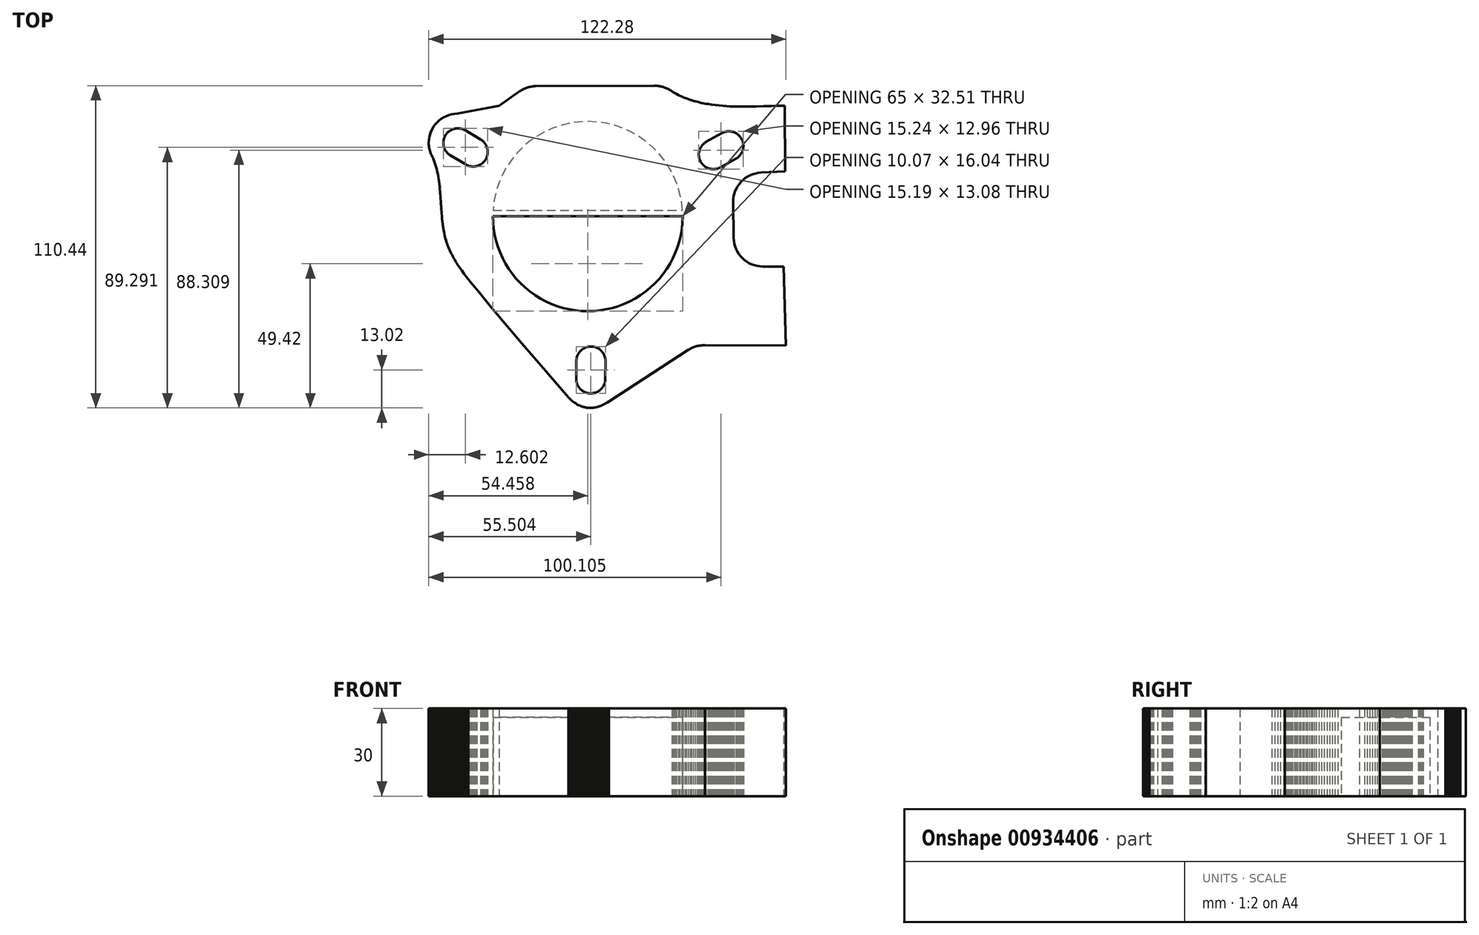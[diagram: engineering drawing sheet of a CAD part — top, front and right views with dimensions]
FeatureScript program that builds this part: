
annotation { "Feature Type Name" : "Feature", "Feature Type Description" : "" }
export const myFeature = defineFeature(function(context is Context, id is Id, definition is map)
    precondition{}
    {
        {
            var Q0;
            Q0=qCreatedBy(makeId("Top.planeOp"),FACE);
            var sketch = newSketch(context, id + "F0", { "sketchPlane" : qUnion([Q0])});
            skArc(sketch, "E0", {"start": v(-6.68, 42.95) * mm, "mid": v(-29.66, 33.43) * mm, "end": v(-39.18, 10.45) * mm});
            skArc(sketch, "E1", {"start": v(-39.18, 10.45) * mm, "mid": v(-29.66, -12.54) * mm, "end": v(-6.68, -22.05) * mm});
            skArc(sketch, "E2", {"start": v(-6.68, -22.05) * mm, "mid": v(16.3, -12.54) * mm, "end": v(25.82, 10.45) * mm});
            skArc(sketch, "E3", {"start": v(25.82, 10.45) * mm, "mid": v(16.3, 33.43) * mm, "end": v(-6.68, 42.95) * mm});
            skLineSegment(sketch, "E4", {"start": v(38.78, 27.25) * mm, "end": v(44.05, 30.21) * mm});
            skLineSegment(sketch, "E5", {"start": v(44.05, 30.21) * mm, "end": v(44.26, 30.34) * mm});
            skLineSegment(sketch, "E6", {"start": v(44.26, 30.34) * mm, "end": v(44.46, 30.47) * mm});
            skLineSegment(sketch, "E7", {"start": v(44.46, 30.47) * mm, "end": v(44.65, 30.61) * mm});
            skLineSegment(sketch, "E8", {"start": v(44.65, 30.61) * mm, "end": v(44.84, 30.76) * mm});
            skLineSegment(sketch, "E9", {"start": v(44.84, 30.76) * mm, "end": v(45.02, 30.92) * mm});
            skLineSegment(sketch, "E10", {"start": v(45.02, 30.92) * mm, "end": v(45.2, 31.1) * mm});
            skLineSegment(sketch, "E11", {"start": v(45.2, 31.1) * mm, "end": v(45.35, 31.27) * mm});
            skLineSegment(sketch, "E12", {"start": v(45.35, 31.27) * mm, "end": v(45.51, 31.45) * mm});
            skLineSegment(sketch, "E13", {"start": v(45.51, 31.45) * mm, "end": v(45.66, 31.65) * mm});
            skLineSegment(sketch, "E14", {"start": v(45.66, 31.65) * mm, "end": v(45.8, 31.85) * mm});
            skLineSegment(sketch, "E15", {"start": v(45.8, 31.85) * mm, "end": v(45.93, 32.06) * mm});
            skLineSegment(sketch, "E16", {"start": v(45.93, 32.06) * mm, "end": v(46.04, 32.28) * mm});
            skLineSegment(sketch, "E17", {"start": v(46.04, 32.28) * mm, "end": v(46.15, 32.5) * mm});
            skLineSegment(sketch, "E18", {"start": v(46.15, 32.5) * mm, "end": v(46.25, 32.74) * mm});
            skLineSegment(sketch, "E19", {"start": v(46.25, 32.74) * mm, "end": v(46.34, 32.98) * mm});
            skLineSegment(sketch, "E20", {"start": v(46.34, 32.98) * mm, "end": v(46.41, 33.22) * mm});
            skArc(sketch, "E21", {"start": v(46.41, 33.22) * mm, "mid": v(45.96, 37.02) * mm, "end": v(42.95, 39.39) * mm});
            skLineSegment(sketch, "E22", {"start": v(42.95, 39.39) * mm, "end": v(42.7, 39.45) * mm});
            skLineSegment(sketch, "E23", {"start": v(42.7, 39.45) * mm, "end": v(42.45, 39.5) * mm});
            skLineSegment(sketch, "E24", {"start": v(42.45, 39.5) * mm, "end": v(42.2, 39.54) * mm});
            skLineSegment(sketch, "E25", {"start": v(42.2, 39.54) * mm, "end": v(41.95, 39.56) * mm});
            skLineSegment(sketch, "E26", {"start": v(41.95, 39.56) * mm, "end": v(41.7, 39.57) * mm});
            skLineSegment(sketch, "E27", {"start": v(41.7, 39.57) * mm, "end": v(41.46, 39.57) * mm});
            skLineSegment(sketch, "E28", {"start": v(41.46, 39.57) * mm, "end": v(41.21, 39.56) * mm});
            skLineSegment(sketch, "E29", {"start": v(41.21, 39.56) * mm, "end": v(40.97, 39.53) * mm});
            skLineSegment(sketch, "E30", {"start": v(40.97, 39.53) * mm, "end": v(40.73, 39.5) * mm});
            skLineSegment(sketch, "E31", {"start": v(40.73, 39.5) * mm, "end": v(40.49, 39.45) * mm});
            skLineSegment(sketch, "E32", {"start": v(40.49, 39.45) * mm, "end": v(40.26, 39.39) * mm});
            skLineSegment(sketch, "E33", {"start": v(40.26, 39.39) * mm, "end": v(40.03, 39.32) * mm});
            skLineSegment(sketch, "E34", {"start": v(40.03, 39.32) * mm, "end": v(39.8, 39.24) * mm});
            skLineSegment(sketch, "E35", {"start": v(39.8, 39.24) * mm, "end": v(39.58, 39.14) * mm});
            skLineSegment(sketch, "E36", {"start": v(39.58, 39.14) * mm, "end": v(39.36, 39.04) * mm});
            skLineSegment(sketch, "E37", {"start": v(39.36, 39.04) * mm, "end": v(39.15, 38.93) * mm});
            skLineSegment(sketch, "E38", {"start": v(39.15, 38.93) * mm, "end": v(33.88, 35.97) * mm});
            skLineSegment(sketch, "E39", {"start": v(33.88, 35.97) * mm, "end": v(33.67, 35.84) * mm});
            skLineSegment(sketch, "E40", {"start": v(33.67, 35.84) * mm, "end": v(33.47, 35.71) * mm});
            skLineSegment(sketch, "E41", {"start": v(33.47, 35.71) * mm, "end": v(33.28, 35.57) * mm});
            skLineSegment(sketch, "E42", {"start": v(33.28, 35.57) * mm, "end": v(33.1, 35.42) * mm});
            skLineSegment(sketch, "E43", {"start": v(33.1, 35.42) * mm, "end": v(32.91, 35.26) * mm});
            skLineSegment(sketch, "E44", {"start": v(32.91, 35.26) * mm, "end": v(32.74, 35.09) * mm});
            skLineSegment(sketch, "E45", {"start": v(32.74, 35.09) * mm, "end": v(32.57, 34.9) * mm});
            skLineSegment(sketch, "E46", {"start": v(32.57, 34.9) * mm, "end": v(32.42, 34.72) * mm});
            skLineSegment(sketch, "E47", {"start": v(32.42, 34.72) * mm, "end": v(32.27, 34.53) * mm});
            skLineSegment(sketch, "E48", {"start": v(32.27, 34.53) * mm, "end": v(32.13, 34.33) * mm});
            skLineSegment(sketch, "E49", {"start": v(32.13, 34.33) * mm, "end": v(32, 34.12) * mm});
            skLineSegment(sketch, "E50", {"start": v(32, 34.12) * mm, "end": v(31.88, 33.9) * mm});
            skLineSegment(sketch, "E51", {"start": v(31.88, 33.9) * mm, "end": v(31.78, 33.67) * mm});
            skLineSegment(sketch, "E52", {"start": v(31.78, 33.67) * mm, "end": v(31.68, 33.44) * mm});
            skLineSegment(sketch, "E53", {"start": v(31.68, 33.44) * mm, "end": v(31.6, 33.2) * mm});
            skLineSegment(sketch, "E54", {"start": v(31.6, 33.2) * mm, "end": v(31.52, 32.96) * mm});
            skArc(sketch, "E55", {"start": v(31.52, 32.96) * mm, "mid": v(31.97, 29.16) * mm, "end": v(34.98, 26.8) * mm});
            skLineSegment(sketch, "E56", {"start": v(34.98, 26.8) * mm, "end": v(35.23, 26.73) * mm});
            skLineSegment(sketch, "E57", {"start": v(35.23, 26.73) * mm, "end": v(35.48, 26.68) * mm});
            skLineSegment(sketch, "E58", {"start": v(35.48, 26.68) * mm, "end": v(35.73, 26.64) * mm});
            skLineSegment(sketch, "E59", {"start": v(35.73, 26.64) * mm, "end": v(35.98, 26.62) * mm});
            skLineSegment(sketch, "E60", {"start": v(35.98, 26.62) * mm, "end": v(36.23, 26.6) * mm});
            skLineSegment(sketch, "E61", {"start": v(36.23, 26.6) * mm, "end": v(36.47, 26.6) * mm});
            skLineSegment(sketch, "E62", {"start": v(36.47, 26.6) * mm, "end": v(36.72, 26.62) * mm});
            skLineSegment(sketch, "E63", {"start": v(36.72, 26.62) * mm, "end": v(36.96, 26.65) * mm});
            skLineSegment(sketch, "E64", {"start": v(36.96, 26.65) * mm, "end": v(37.2, 26.68) * mm});
            skLineSegment(sketch, "E65", {"start": v(37.2, 26.68) * mm, "end": v(37.44, 26.73) * mm});
            skLineSegment(sketch, "E66", {"start": v(37.44, 26.73) * mm, "end": v(37.67, 26.8) * mm});
            skLineSegment(sketch, "E67", {"start": v(37.67, 26.8) * mm, "end": v(37.9, 26.86) * mm});
            skLineSegment(sketch, "E68", {"start": v(37.9, 26.86) * mm, "end": v(38.13, 26.94) * mm});
            skLineSegment(sketch, "E69", {"start": v(38.13, 26.94) * mm, "end": v(38.35, 27.03) * mm});
            skLineSegment(sketch, "E70", {"start": v(38.35, 27.03) * mm, "end": v(38.57, 27.14) * mm});
            skLineSegment(sketch, "E71", {"start": v(38.57, 27.14) * mm, "end": v(38.78, 27.25) * mm});
            skLineSegment(sketch, "E72", {"start": v(-10.6, -39.12) * mm, "end": v(-10.67, -45.17) * mm});
            skLineSegment(sketch, "E73", {"start": v(-10.67, -45.17) * mm, "end": v(-10.67, -45.4) * mm});
            skLineSegment(sketch, "E74", {"start": v(-10.67, -45.4) * mm, "end": v(-10.65, -45.65) * mm});
            skLineSegment(sketch, "E75", {"start": v(-10.65, -45.65) * mm, "end": v(-10.63, -45.88) * mm});
            skLineSegment(sketch, "E76", {"start": v(-10.63, -45.88) * mm, "end": v(-10.59, -46.12) * mm});
            skLineSegment(sketch, "E77", {"start": v(-10.59, -46.12) * mm, "end": v(-10.54, -46.36) * mm});
            skLineSegment(sketch, "E78", {"start": v(-10.54, -46.36) * mm, "end": v(-10.48, -46.6) * mm});
            skLineSegment(sketch, "E79", {"start": v(-10.48, -46.6) * mm, "end": v(-10.4, -46.82) * mm});
            skLineSegment(sketch, "E80", {"start": v(-10.4, -46.82) * mm, "end": v(-10.33, -47.05) * mm});
            skLineSegment(sketch, "E81", {"start": v(-10.33, -47.05) * mm, "end": v(-10.23, -47.28) * mm});
            skLineSegment(sketch, "E82", {"start": v(-10.23, -47.28) * mm, "end": v(-10.12, -47.5) * mm});
            skLineSegment(sketch, "E83", {"start": v(-10.12, -47.5) * mm, "end": v(-10, -47.71) * mm});
            skLineSegment(sketch, "E84", {"start": v(-10, -47.71) * mm, "end": v(-9.88, -47.93) * mm});
            skLineSegment(sketch, "E85", {"start": v(-9.88, -47.93) * mm, "end": v(-9.74, -48.13) * mm});
            skLineSegment(sketch, "E86", {"start": v(-9.74, -48.13) * mm, "end": v(-9.58, -48.33) * mm});
            skLineSegment(sketch, "E87", {"start": v(-9.58, -48.33) * mm, "end": v(-9.42, -48.53) * mm});
            skLineSegment(sketch, "E88", {"start": v(-9.42, -48.53) * mm, "end": v(-9.25, -48.72) * mm});
            skArc(sketch, "E89", {"start": v(-9.25, -48.72) * mm, "mid": v(-5.73, -50.22) * mm, "end": v(-2.17, -48.8) * mm});
            skLineSegment(sketch, "E90", {"start": v(-2.17, -48.8) * mm, "end": v(-2, -48.61) * mm});
            skLineSegment(sketch, "E91", {"start": v(-2, -48.61) * mm, "end": v(-1.83, -48.42) * mm});
            skLineSegment(sketch, "E92", {"start": v(-1.83, -48.42) * mm, "end": v(-1.67, -48.22) * mm});
            skLineSegment(sketch, "E93", {"start": v(-1.67, -48.22) * mm, "end": v(-1.53, -48.02) * mm});
            skLineSegment(sketch, "E94", {"start": v(-1.53, -48.02) * mm, "end": v(-1.4, -47.81) * mm});
            skLineSegment(sketch, "E95", {"start": v(-1.4, -47.81) * mm, "end": v(-1.27, -47.6) * mm});
            skLineSegment(sketch, "E96", {"start": v(-1.27, -47.6) * mm, "end": v(-1.16, -47.38) * mm});
            skLineSegment(sketch, "E97", {"start": v(-1.16, -47.38) * mm, "end": v(-1.06, -47.16) * mm});
            skLineSegment(sketch, "E98", {"start": v(-1.06, -47.16) * mm, "end": v(-0.97, -46.93) * mm});
            skLineSegment(sketch, "E99", {"start": v(-0.97, -46.93) * mm, "end": v(-0.9, -46.7) * mm});
            skLineSegment(sketch, "E100", {"start": v(-0.9, -46.7) * mm, "end": v(-0.83, -46.47) * mm});
            skLineSegment(sketch, "E101", {"start": v(-0.83, -46.47) * mm, "end": v(-0.77, -46.23) * mm});
            skLineSegment(sketch, "E102", {"start": v(-0.77, -46.23) * mm, "end": v(-0.73, -46) * mm});
            skLineSegment(sketch, "E103", {"start": v(-0.73, -46) * mm, "end": v(-0.7, -45.76) * mm});
            skLineSegment(sketch, "E104", {"start": v(-0.7, -45.76) * mm, "end": v(-0.68, -45.52) * mm});
            skLineSegment(sketch, "E105", {"start": v(-0.68, -45.52) * mm, "end": v(-0.67, -45.28) * mm});
            skLineSegment(sketch, "E106", {"start": v(-0.67, -45.28) * mm, "end": v(-0.6, -39.23) * mm});
            skLineSegment(sketch, "E107", {"start": v(-0.6, -39.23) * mm, "end": v(-0.6, -39) * mm});
            skLineSegment(sketch, "E108", {"start": v(-0.6, -39) * mm, "end": v(-0.62, -38.75) * mm});
            skLineSegment(sketch, "E109", {"start": v(-0.62, -38.75) * mm, "end": v(-0.65, -38.51) * mm});
            skLineSegment(sketch, "E110", {"start": v(-0.65, -38.51) * mm, "end": v(-0.68, -38.28) * mm});
            skLineSegment(sketch, "E111", {"start": v(-0.68, -38.28) * mm, "end": v(-0.73, -38.04) * mm});
            skLineSegment(sketch, "E112", {"start": v(-0.73, -38.04) * mm, "end": v(-0.8, -37.8) * mm});
            skLineSegment(sketch, "E113", {"start": v(-0.8, -37.8) * mm, "end": v(-0.86, -37.58) * mm});
            skLineSegment(sketch, "E114", {"start": v(-0.86, -37.58) * mm, "end": v(-0.95, -37.35) * mm});
            skLineSegment(sketch, "E115", {"start": v(-0.95, -37.35) * mm, "end": v(-1.04, -37.12) * mm});
            skLineSegment(sketch, "E116", {"start": v(-1.04, -37.12) * mm, "end": v(-1.15, -36.9) * mm});
            skLineSegment(sketch, "E117", {"start": v(-1.15, -36.9) * mm, "end": v(-1.27, -36.68) * mm});
            skLineSegment(sketch, "E118", {"start": v(-1.27, -36.68) * mm, "end": v(-1.4, -36.47) * mm});
            skLineSegment(sketch, "E119", {"start": v(-1.4, -36.47) * mm, "end": v(-1.54, -36.27) * mm});
            skLineSegment(sketch, "E120", {"start": v(-1.54, -36.27) * mm, "end": v(-1.69, -36.06) * mm});
            skLineSegment(sketch, "E121", {"start": v(-1.69, -36.06) * mm, "end": v(-1.85, -35.87) * mm});
            skLineSegment(sketch, "E122", {"start": v(-1.85, -35.87) * mm, "end": v(-2.03, -35.68) * mm});
            skArc(sketch, "E123", {"start": v(-2.03, -35.68) * mm, "mid": v(-5.55, -34.18) * mm, "end": v(-9.1, -35.6) * mm});
            skLineSegment(sketch, "E124", {"start": v(-9.1, -35.6) * mm, "end": v(-9.28, -35.79) * mm});
            skLineSegment(sketch, "E125", {"start": v(-9.28, -35.79) * mm, "end": v(-9.45, -35.98) * mm});
            skLineSegment(sketch, "E126", {"start": v(-9.45, -35.98) * mm, "end": v(-9.6, -36.18) * mm});
            skLineSegment(sketch, "E127", {"start": v(-9.6, -36.18) * mm, "end": v(-9.75, -36.38) * mm});
            skLineSegment(sketch, "E128", {"start": v(-9.75, -36.38) * mm, "end": v(-9.88, -36.59) * mm});
            skLineSegment(sketch, "E129", {"start": v(-9.88, -36.59) * mm, "end": v(-10, -36.8) * mm});
            skLineSegment(sketch, "E130", {"start": v(-10, -36.8) * mm, "end": v(-10.12, -37.02) * mm});
            skLineSegment(sketch, "E131", {"start": v(-10.12, -37.02) * mm, "end": v(-10.22, -37.24) * mm});
            skLineSegment(sketch, "E132", {"start": v(-10.22, -37.24) * mm, "end": v(-10.3, -37.47) * mm});
            skLineSegment(sketch, "E133", {"start": v(-10.3, -37.47) * mm, "end": v(-10.38, -37.7) * mm});
            skLineSegment(sketch, "E134", {"start": v(-10.38, -37.7) * mm, "end": v(-10.45, -37.93) * mm});
            skLineSegment(sketch, "E135", {"start": v(-10.45, -37.93) * mm, "end": v(-10.5, -38.17) * mm});
            skLineSegment(sketch, "E136", {"start": v(-10.5, -38.17) * mm, "end": v(-10.54, -38.4) * mm});
            skLineSegment(sketch, "E137", {"start": v(-10.54, -38.4) * mm, "end": v(-10.57, -38.64) * mm});
            skLineSegment(sketch, "E138", {"start": v(-10.57, -38.64) * mm, "end": v(-10.6, -38.88) * mm});
            skLineSegment(sketch, "E139", {"start": v(-10.6, -38.88) * mm, "end": v(-10.6, -39.12) * mm});
            skLineSegment(sketch, "E140", {"start": v(-43.39, 36.83) * mm, "end": v(-48.6, 39.91) * mm});
            skLineSegment(sketch, "E141", {"start": v(-48.6, 39.91) * mm, "end": v(-48.8, 40.03) * mm});
            skLineSegment(sketch, "E142", {"start": v(-48.8, 40.03) * mm, "end": v(-49.01, 40.14) * mm});
            skLineSegment(sketch, "E143", {"start": v(-49.01, 40.14) * mm, "end": v(-49.23, 40.23) * mm});
            skLineSegment(sketch, "E144", {"start": v(-49.23, 40.23) * mm, "end": v(-49.46, 40.32) * mm});
            skLineSegment(sketch, "E145", {"start": v(-49.46, 40.32) * mm, "end": v(-49.69, 40.4) * mm});
            skLineSegment(sketch, "E146", {"start": v(-49.69, 40.4) * mm, "end": v(-49.92, 40.46) * mm});
            skLineSegment(sketch, "E147", {"start": v(-49.92, 40.46) * mm, "end": v(-50.16, 40.52) * mm});
            skLineSegment(sketch, "E148", {"start": v(-50.16, 40.52) * mm, "end": v(-50.4, 40.56) * mm});
            skLineSegment(sketch, "E149", {"start": v(-50.4, 40.56) * mm, "end": v(-50.64, 40.59) * mm});
            skLineSegment(sketch, "E150", {"start": v(-50.64, 40.59) * mm, "end": v(-50.88, 40.6) * mm});
            skLineSegment(sketch, "E151", {"start": v(-50.88, 40.6) * mm, "end": v(-51.13, 40.61) * mm});
            skLineSegment(sketch, "E152", {"start": v(-51.13, 40.61) * mm, "end": v(-51.38, 40.6) * mm});
            skLineSegment(sketch, "E153", {"start": v(-51.38, 40.6) * mm, "end": v(-51.63, 40.59) * mm});
            skLineSegment(sketch, "E154", {"start": v(-51.63, 40.59) * mm, "end": v(-51.88, 40.56) * mm});
            skLineSegment(sketch, "E155", {"start": v(-51.88, 40.56) * mm, "end": v(-52.13, 40.51) * mm});
            skLineSegment(sketch, "E156", {"start": v(-52.13, 40.51) * mm, "end": v(-52.38, 40.46) * mm});
            skArc(sketch, "E157", {"start": v(-52.38, 40.46) * mm, "mid": v(-55.44, 38.16) * mm, "end": v(-55.98, 34.37) * mm});
            skLineSegment(sketch, "E158", {"start": v(-55.98, 34.37) * mm, "end": v(-55.91, 34.12) * mm});
            skLineSegment(sketch, "E159", {"start": v(-55.91, 34.12) * mm, "end": v(-55.83, 33.88) * mm});
            skLineSegment(sketch, "E160", {"start": v(-55.83, 33.88) * mm, "end": v(-55.74, 33.65) * mm});
            skLineSegment(sketch, "E161", {"start": v(-55.74, 33.65) * mm, "end": v(-55.63, 33.42) * mm});
            skLineSegment(sketch, "E162", {"start": v(-55.63, 33.42) * mm, "end": v(-55.52, 33.2) * mm});
            skLineSegment(sketch, "E163", {"start": v(-55.52, 33.2) * mm, "end": v(-55.4, 32.99) * mm});
            skLineSegment(sketch, "E164", {"start": v(-55.4, 32.99) * mm, "end": v(-55.26, 32.78) * mm});
            skLineSegment(sketch, "E165", {"start": v(-55.26, 32.78) * mm, "end": v(-55.12, 32.58) * mm});
            skLineSegment(sketch, "E166", {"start": v(-55.12, 32.58) * mm, "end": v(-54.97, 32.4) * mm});
            skLineSegment(sketch, "E167", {"start": v(-54.97, 32.4) * mm, "end": v(-54.8, 32.21) * mm});
            skLineSegment(sketch, "E168", {"start": v(-54.8, 32.21) * mm, "end": v(-54.64, 32.04) * mm});
            skLineSegment(sketch, "E169", {"start": v(-54.64, 32.04) * mm, "end": v(-54.46, 31.88) * mm});
            skLineSegment(sketch, "E170", {"start": v(-54.46, 31.88) * mm, "end": v(-54.28, 31.72) * mm});
            skLineSegment(sketch, "E171", {"start": v(-54.28, 31.72) * mm, "end": v(-54.09, 31.57) * mm});
            skLineSegment(sketch, "E172", {"start": v(-54.09, 31.57) * mm, "end": v(-53.9, 31.44) * mm});
            skLineSegment(sketch, "E173", {"start": v(-53.9, 31.44) * mm, "end": v(-53.69, 31.3) * mm});
            skLineSegment(sketch, "E174", {"start": v(-53.69, 31.3) * mm, "end": v(-48.49, 28.23) * mm});
            skLineSegment(sketch, "E175", {"start": v(-48.49, 28.23) * mm, "end": v(-48.28, 28.11) * mm});
            skLineSegment(sketch, "E176", {"start": v(-48.28, 28.11) * mm, "end": v(-48.06, 28) * mm});
            skLineSegment(sketch, "E177", {"start": v(-48.06, 28) * mm, "end": v(-47.84, 27.9) * mm});
            skLineSegment(sketch, "E178", {"start": v(-47.84, 27.9) * mm, "end": v(-47.62, 27.82) * mm});
            skLineSegment(sketch, "E179", {"start": v(-47.62, 27.82) * mm, "end": v(-47.39, 27.74) * mm});
            skLineSegment(sketch, "E180", {"start": v(-47.39, 27.74) * mm, "end": v(-47.16, 27.68) * mm});
            skLineSegment(sketch, "E181", {"start": v(-47.16, 27.68) * mm, "end": v(-46.92, 27.63) * mm});
            skLineSegment(sketch, "E182", {"start": v(-46.92, 27.63) * mm, "end": v(-46.68, 27.58) * mm});
            skLineSegment(sketch, "E183", {"start": v(-46.68, 27.58) * mm, "end": v(-46.44, 27.55) * mm});
            skLineSegment(sketch, "E184", {"start": v(-46.44, 27.55) * mm, "end": v(-46.2, 27.54) * mm});
            skLineSegment(sketch, "E185", {"start": v(-46.2, 27.54) * mm, "end": v(-45.95, 27.53) * mm});
            skLineSegment(sketch, "E186", {"start": v(-45.95, 27.53) * mm, "end": v(-45.7, 27.53) * mm});
            skLineSegment(sketch, "E187", {"start": v(-45.7, 27.53) * mm, "end": v(-45.45, 27.55) * mm});
            skLineSegment(sketch, "E188", {"start": v(-45.45, 27.55) * mm, "end": v(-45.2, 27.58) * mm});
            skLineSegment(sketch, "E189", {"start": v(-45.2, 27.58) * mm, "end": v(-44.95, 27.63) * mm});
            skLineSegment(sketch, "E190", {"start": v(-44.95, 27.63) * mm, "end": v(-44.7, 27.69) * mm});
            skArc(sketch, "E191", {"start": v(-44.7, 27.69) * mm, "mid": v(-41.64, 29.98) * mm, "end": v(-41.1, 33.77) * mm});
            skLineSegment(sketch, "E192", {"start": v(-41.1, 33.77) * mm, "end": v(-41.16, 34.02) * mm});
            skLineSegment(sketch, "E193", {"start": v(-41.16, 34.02) * mm, "end": v(-41.25, 34.26) * mm});
            skLineSegment(sketch, "E194", {"start": v(-41.25, 34.26) * mm, "end": v(-41.34, 34.5) * mm});
            skLineSegment(sketch, "E195", {"start": v(-41.34, 34.5) * mm, "end": v(-41.44, 34.72) * mm});
            skLineSegment(sketch, "E196", {"start": v(-41.44, 34.72) * mm, "end": v(-41.56, 34.94) * mm});
            skLineSegment(sketch, "E197", {"start": v(-41.56, 34.94) * mm, "end": v(-41.68, 35.15) * mm});
            skLineSegment(sketch, "E198", {"start": v(-41.68, 35.15) * mm, "end": v(-41.81, 35.36) * mm});
            skLineSegment(sketch, "E199", {"start": v(-41.81, 35.36) * mm, "end": v(-41.96, 35.56) * mm});
            skLineSegment(sketch, "E200", {"start": v(-41.96, 35.56) * mm, "end": v(-42.1, 35.75) * mm});
            skLineSegment(sketch, "E201", {"start": v(-42.1, 35.75) * mm, "end": v(-42.27, 35.93) * mm});
            skLineSegment(sketch, "E202", {"start": v(-42.27, 35.93) * mm, "end": v(-42.44, 36.1) * mm});
            skLineSegment(sketch, "E203", {"start": v(-42.44, 36.1) * mm, "end": v(-42.61, 36.27) * mm});
            skLineSegment(sketch, "E204", {"start": v(-42.61, 36.27) * mm, "end": v(-42.8, 36.42) * mm});
            skLineSegment(sketch, "E205", {"start": v(-42.8, 36.42) * mm, "end": v(-42.99, 36.57) * mm});
            skLineSegment(sketch, "E206", {"start": v(-42.99, 36.57) * mm, "end": v(-43.19, 36.7) * mm});
            skLineSegment(sketch, "E207", {"start": v(-43.19, 36.7) * mm, "end": v(-43.39, 36.83) * mm});
            skLineSegment(sketch, "E208", {"start": v(-51.31, 45.6) * mm, "end": v(-37.06, 48.31) * mm});
            skLineSegment(sketch, "E209", {"start": v(-37.06, 48.31) * mm, "end": v(-30.05, 53.23) * mm});
            skArc(sketch, "E210", {"start": v(-30.05, 53.23) * mm, "mid": v(-27.36, 54.56) * mm, "end": v(-24.4, 55.04) * mm});
            skLineSegment(sketch, "E211", {"start": v(-24.4, 55.04) * mm, "end": v(16.1, 55.22) * mm});
            skArc(sketch, "E212", {"start": v(16.1, 55.22) * mm, "mid": v(18.95, 54.82) * mm, "end": v(21.58, 53.62) * mm});
            skLineSegment(sketch, "E213", {"start": v(21.58, 53.62) * mm, "end": v(22.1, 53.28) * mm});
            skLineSegment(sketch, "E214", {"start": v(22.1, 53.28) * mm, "end": v(22.64, 52.96) * mm});
            skLineSegment(sketch, "E215", {"start": v(22.64, 52.96) * mm, "end": v(23.18, 52.65) * mm});
            skLineSegment(sketch, "E216", {"start": v(23.18, 52.65) * mm, "end": v(23.73, 52.35) * mm});
            skLineSegment(sketch, "E217", {"start": v(23.73, 52.35) * mm, "end": v(24.29, 52.07) * mm});
            skLineSegment(sketch, "E218", {"start": v(24.29, 52.07) * mm, "end": v(24.85, 51.8) * mm});
            skLineSegment(sketch, "E219", {"start": v(24.85, 51.8) * mm, "end": v(25.41, 51.53) * mm});
            skLineSegment(sketch, "E220", {"start": v(25.41, 51.53) * mm, "end": v(25.98, 51.29) * mm});
            skLineSegment(sketch, "E221", {"start": v(25.98, 51.29) * mm, "end": v(26.56, 51.05) * mm});
            skLineSegment(sketch, "E222", {"start": v(26.56, 51.05) * mm, "end": v(27.14, 50.82) * mm});
            skLineSegment(sketch, "E223", {"start": v(27.14, 50.82) * mm, "end": v(27.73, 50.6) * mm});
            skLineSegment(sketch, "E224", {"start": v(27.73, 50.6) * mm, "end": v(28.32, 50.4) * mm});
            skLineSegment(sketch, "E225", {"start": v(28.32, 50.4) * mm, "end": v(28.91, 50.21) * mm});
            skLineSegment(sketch, "E226", {"start": v(28.91, 50.21) * mm, "end": v(29.51, 50.03) * mm});
            skLineSegment(sketch, "E227", {"start": v(29.51, 50.03) * mm, "end": v(30.11, 49.86) * mm});
            skLineSegment(sketch, "E228", {"start": v(30.11, 49.86) * mm, "end": v(30.72, 49.7) * mm});
            skLineSegment(sketch, "E229", {"start": v(30.72, 49.7) * mm, "end": v(31.33, 49.54) * mm});
            skLineSegment(sketch, "E230", {"start": v(31.33, 49.54) * mm, "end": v(31.94, 49.4) * mm});
            skLineSegment(sketch, "E231", {"start": v(31.94, 49.4) * mm, "end": v(32.56, 49.26) * mm});
            skLineSegment(sketch, "E232", {"start": v(32.56, 49.26) * mm, "end": v(33.18, 49.14) * mm});
            skLineSegment(sketch, "E233", {"start": v(33.18, 49.14) * mm, "end": v(33.8, 49.02) * mm});
            skLineSegment(sketch, "E234", {"start": v(33.8, 49.02) * mm, "end": v(34.43, 48.9) * mm});
            skLineSegment(sketch, "E235", {"start": v(34.43, 48.9) * mm, "end": v(35.06, 48.8) * mm});
            skLineSegment(sketch, "E236", {"start": v(35.06, 48.8) * mm, "end": v(35.69, 48.71) * mm});
            skLineSegment(sketch, "E237", {"start": v(35.69, 48.71) * mm, "end": v(36.96, 48.55) * mm});
            skLineSegment(sketch, "E238", {"start": v(36.96, 48.55) * mm, "end": v(38.23, 48.4) * mm});
            skLineSegment(sketch, "E239", {"start": v(38.23, 48.4) * mm, "end": v(39.51, 48.3) * mm});
            skLineSegment(sketch, "E240", {"start": v(39.51, 48.3) * mm, "end": v(40.8, 48.2) * mm});
            skLineSegment(sketch, "E241", {"start": v(40.8, 48.2) * mm, "end": v(42.08, 48.14) * mm});
            skLineSegment(sketch, "E242", {"start": v(42.08, 48.14) * mm, "end": v(43.37, 48.1) * mm});
            skLineSegment(sketch, "E243", {"start": v(43.37, 48.1) * mm, "end": v(44.66, 48.06) * mm});
            skLineSegment(sketch, "E244", {"start": v(44.66, 48.06) * mm, "end": v(45.95, 48.04) * mm});
            skLineSegment(sketch, "E245", {"start": v(45.95, 48.04) * mm, "end": v(47.23, 48.04) * mm});
            skLineSegment(sketch, "E246", {"start": v(47.23, 48.04) * mm, "end": v(48.51, 48.05) * mm});
            skLineSegment(sketch, "E247", {"start": v(48.51, 48.05) * mm, "end": v(51.05, 48.1) * mm});
            skLineSegment(sketch, "E248", {"start": v(51.05, 48.1) * mm, "end": v(53.55, 48.15) * mm});
            skLineSegment(sketch, "E249", {"start": v(53.55, 48.15) * mm, "end": v(56, 48.22) * mm});
            skLineSegment(sketch, "E250", {"start": v(56, 48.22) * mm, "end": v(58.4, 48.27) * mm});
            skLineSegment(sketch, "E251", {"start": v(58.4, 48.27) * mm, "end": v(59.57, 48.29) * mm});
            skLineSegment(sketch, "E252", {"start": v(59.57, 48.29) * mm, "end": v(60.72, 48.3) * mm});
            skLineSegment(sketch, "E253", {"start": v(60.72, 48.3) * mm, "end": v(60.94, 25.8) * mm});
            skLineSegment(sketch, "E254", {"start": v(60.94, 25.8) * mm, "end": v(52.62, 25.41) * mm});
            skArc(sketch, "E255", {"start": v(52.62, 25.41) * mm, "mid": v(45.82, 22.29) * mm, "end": v(43.09, 15.31) * mm});
            skLineSegment(sketch, "E256", {"start": v(43.09, 15.31) * mm, "end": v(43.27, 3.08) * mm});
            skArc(sketch, "E257", {"start": v(43.27, 3.08) * mm, "mid": v(46.26, -3.9) * mm, "end": v(53.31, -6.77) * mm});
            skLineSegment(sketch, "E258", {"start": v(53.31, -6.77) * mm, "end": v(60.41, -6.77) * mm});
            skLineSegment(sketch, "E259", {"start": v(60.41, -6.77) * mm, "end": v(61.14, -33.8) * mm});
            skLineSegment(sketch, "E260", {"start": v(61.14, -33.8) * mm, "end": v(33.46, -33.77) * mm});
            skArc(sketch, "E261", {"start": v(33.46, -33.77) * mm, "mid": v(30.43, -34.12) * mm, "end": v(27.64, -35.38) * mm});
            skLineSegment(sketch, "E262", {"start": v(27.64, -35.38) * mm, "end": v(0.53, -53.07) * mm});
            skLineSegment(sketch, "E263", {"start": v(0.53, -53.07) * mm, "end": v(-0.14, -53.45) * mm});
            skLineSegment(sketch, "E264", {"start": v(-0.14, -53.45) * mm, "end": v(-0.84, -53.83) * mm});
            skLineSegment(sketch, "E265", {"start": v(-0.84, -53.83) * mm, "end": v(-1.2, -54.01) * mm});
            skLineSegment(sketch, "E266", {"start": v(-1.2, -54.01) * mm, "end": v(-1.58, -54.19) * mm});
            skLineSegment(sketch, "E267", {"start": v(-1.58, -54.19) * mm, "end": v(-1.96, -54.36) * mm});
            skLineSegment(sketch, "E268", {"start": v(-1.96, -54.36) * mm, "end": v(-2.34, -54.52) * mm});
            skLineSegment(sketch, "E269", {"start": v(-2.34, -54.52) * mm, "end": v(-2.74, -54.67) * mm});
            skLineSegment(sketch, "E270", {"start": v(-2.74, -54.67) * mm, "end": v(-3.14, -54.8) * mm});
            skLineSegment(sketch, "E271", {"start": v(-3.14, -54.8) * mm, "end": v(-3.54, -54.92) * mm});
            skLineSegment(sketch, "E272", {"start": v(-3.54, -54.92) * mm, "end": v(-3.96, -55.03) * mm});
            skLineSegment(sketch, "E273", {"start": v(-3.96, -55.03) * mm, "end": v(-4.38, -55.1) * mm});
            skLineSegment(sketch, "E274", {"start": v(-4.38, -55.1) * mm, "end": v(-4.8, -55.17) * mm});
            skLineSegment(sketch, "E275", {"start": v(-4.8, -55.17) * mm, "end": v(-5.23, -55.2) * mm});
            skLineSegment(sketch, "E276", {"start": v(-5.23, -55.2) * mm, "end": v(-5.67, -55.22) * mm});
            skLineSegment(sketch, "E277", {"start": v(-5.67, -55.22) * mm, "end": v(-5.96, -55.22) * mm});
            skLineSegment(sketch, "E278", {"start": v(-5.96, -55.22) * mm, "end": v(-6.24, -55.2) * mm});
            skLineSegment(sketch, "E279", {"start": v(-6.24, -55.2) * mm, "end": v(-6.52, -55.18) * mm});
            skLineSegment(sketch, "E280", {"start": v(-6.52, -55.18) * mm, "end": v(-6.8, -55.16) * mm});
            skLineSegment(sketch, "E281", {"start": v(-6.8, -55.16) * mm, "end": v(-7.07, -55.12) * mm});
            skLineSegment(sketch, "E282", {"start": v(-7.07, -55.12) * mm, "end": v(-7.34, -55.07) * mm});
            skLineSegment(sketch, "E283", {"start": v(-7.34, -55.07) * mm, "end": v(-7.6, -55.02) * mm});
            skLineSegment(sketch, "E284", {"start": v(-7.6, -55.02) * mm, "end": v(-7.87, -54.96) * mm});
            skLineSegment(sketch, "E285", {"start": v(-7.87, -54.96) * mm, "end": v(-8.13, -54.9) * mm});
            skLineSegment(sketch, "E286", {"start": v(-8.13, -54.9) * mm, "end": v(-8.39, -54.82) * mm});
            skLineSegment(sketch, "E287", {"start": v(-8.39, -54.82) * mm, "end": v(-8.64, -54.74) * mm});
            skLineSegment(sketch, "E288", {"start": v(-8.64, -54.74) * mm, "end": v(-8.9, -54.65) * mm});
            skLineSegment(sketch, "E289", {"start": v(-8.9, -54.65) * mm, "end": v(-9.38, -54.45) * mm});
            skLineSegment(sketch, "E290", {"start": v(-9.38, -54.45) * mm, "end": v(-9.86, -54.23) * mm});
            skLineSegment(sketch, "E291", {"start": v(-9.86, -54.23) * mm, "end": v(-10.33, -53.98) * mm});
            skLineSegment(sketch, "E292", {"start": v(-10.33, -53.98) * mm, "end": v(-10.8, -53.7) * mm});
            skLineSegment(sketch, "E293", {"start": v(-10.8, -53.7) * mm, "end": v(-11.24, -53.4) * mm});
            skLineSegment(sketch, "E294", {"start": v(-11.24, -53.4) * mm, "end": v(-11.68, -53.1) * mm});
            skLineSegment(sketch, "E295", {"start": v(-11.68, -53.1) * mm, "end": v(-12.1, -52.76) * mm});
            skLineSegment(sketch, "E296", {"start": v(-12.1, -52.76) * mm, "end": v(-12.52, -52.4) * mm});
            skLineSegment(sketch, "E297", {"start": v(-12.52, -52.4) * mm, "end": v(-12.93, -52.03) * mm});
            skLineSegment(sketch, "E298", {"start": v(-12.93, -52.03) * mm, "end": v(-13.34, -51.64) * mm});
            skLineSegment(sketch, "E299", {"start": v(-13.34, -51.64) * mm, "end": v(-21.09, -42.65) * mm});
            skLineSegment(sketch, "E300", {"start": v(-21.09, -42.65) * mm, "end": v(-25.15, -37.91) * mm});
            skLineSegment(sketch, "E301", {"start": v(-25.15, -37.91) * mm, "end": v(-29.3, -33.06) * mm});
            skLineSegment(sketch, "E302", {"start": v(-29.3, -33.06) * mm, "end": v(-33.5, -28.12) * mm});
            skLineSegment(sketch, "E303", {"start": v(-33.5, -28.12) * mm, "end": v(-35.6, -25.63) * mm});
            skLineSegment(sketch, "E304", {"start": v(-35.6, -25.63) * mm, "end": v(-37.7, -23.12) * mm});
            skLineSegment(sketch, "E305", {"start": v(-37.7, -23.12) * mm, "end": v(-39.79, -20.61) * mm});
            skLineSegment(sketch, "E306", {"start": v(-39.79, -20.61) * mm, "end": v(-41.88, -18.1) * mm});
            skLineSegment(sketch, "E307", {"start": v(-41.88, -18.1) * mm, "end": v(-43.95, -15.58) * mm});
            skLineSegment(sketch, "E308", {"start": v(-43.95, -15.58) * mm, "end": v(-46, -13.07) * mm});
            skLineSegment(sketch, "E309", {"start": v(-46, -13.07) * mm, "end": v(-46.77, -12.12) * mm});
            skLineSegment(sketch, "E310", {"start": v(-46.77, -12.12) * mm, "end": v(-47.53, -11.16) * mm});
            skLineSegment(sketch, "E311", {"start": v(-47.53, -11.16) * mm, "end": v(-48.3, -10.19) * mm});
            skLineSegment(sketch, "E312", {"start": v(-48.3, -10.19) * mm, "end": v(-49.04, -9.2) * mm});
            skLineSegment(sketch, "E313", {"start": v(-49.04, -9.2) * mm, "end": v(-49.78, -8.19) * mm});
            skLineSegment(sketch, "E314", {"start": v(-49.78, -8.19) * mm, "end": v(-50.5, -7.17) * mm});
            skLineSegment(sketch, "E315", {"start": v(-50.5, -7.17) * mm, "end": v(-50.85, -6.65) * mm});
            skLineSegment(sketch, "E316", {"start": v(-50.85, -6.65) * mm, "end": v(-51.2, -6.13) * mm});
            skLineSegment(sketch, "E317", {"start": v(-51.2, -6.13) * mm, "end": v(-51.53, -5.6) * mm});
            skLineSegment(sketch, "E318", {"start": v(-51.53, -5.6) * mm, "end": v(-51.86, -5.08) * mm});
            skLineSegment(sketch, "E319", {"start": v(-51.86, -5.08) * mm, "end": v(-52.18, -4.54) * mm});
            skLineSegment(sketch, "E320", {"start": v(-52.18, -4.54) * mm, "end": v(-52.5, -4) * mm});
            skLineSegment(sketch, "E321", {"start": v(-52.5, -4) * mm, "end": v(-52.8, -3.46) * mm});
            skLineSegment(sketch, "E322", {"start": v(-52.8, -3.46) * mm, "end": v(-53.1, -2.91) * mm});
            skLineSegment(sketch, "E323", {"start": v(-53.1, -2.91) * mm, "end": v(-53.38, -2.36) * mm});
            skLineSegment(sketch, "E324", {"start": v(-53.38, -2.36) * mm, "end": v(-53.65, -1.8) * mm});
            skLineSegment(sketch, "E325", {"start": v(-53.65, -1.8) * mm, "end": v(-53.92, -1.24) * mm});
            skLineSegment(sketch, "E326", {"start": v(-53.92, -1.24) * mm, "end": v(-54.17, -0.67) * mm});
            skLineSegment(sketch, "E327", {"start": v(-54.17, -0.67) * mm, "end": v(-54.4, -0.1) * mm});
            skLineSegment(sketch, "E328", {"start": v(-54.4, -0.1) * mm, "end": v(-54.63, 0.48) * mm});
            skLineSegment(sketch, "E329", {"start": v(-54.63, 0.48) * mm, "end": v(-54.85, 1.06) * mm});
            skLineSegment(sketch, "E330", {"start": v(-54.85, 1.06) * mm, "end": v(-55.05, 1.64) * mm});
            skLineSegment(sketch, "E331", {"start": v(-55.05, 1.64) * mm, "end": v(-55.23, 2.24) * mm});
            skLineSegment(sketch, "E332", {"start": v(-55.23, 2.24) * mm, "end": v(-55.4, 2.83) * mm});
            skLineSegment(sketch, "E333", {"start": v(-55.4, 2.83) * mm, "end": v(-55.55, 3.44) * mm});
            skLineSegment(sketch, "E334", {"start": v(-55.55, 3.44) * mm, "end": v(-55.7, 4.05) * mm});
            skLineSegment(sketch, "E335", {"start": v(-55.7, 4.05) * mm, "end": v(-55.87, 4.95) * mm});
            skLineSegment(sketch, "E336", {"start": v(-55.87, 4.95) * mm, "end": v(-56.04, 5.87) * mm});
            skLineSegment(sketch, "E337", {"start": v(-56.04, 5.87) * mm, "end": v(-56.18, 6.8) * mm});
            skLineSegment(sketch, "E338", {"start": v(-56.18, 6.8) * mm, "end": v(-56.31, 7.72) * mm});
            skLineSegment(sketch, "E339", {"start": v(-56.31, 7.72) * mm, "end": v(-56.43, 8.64) * mm});
            skLineSegment(sketch, "E340", {"start": v(-56.43, 8.64) * mm, "end": v(-56.53, 9.58) * mm});
            skLineSegment(sketch, "E341", {"start": v(-56.53, 9.58) * mm, "end": v(-56.62, 10.5) * mm});
            skLineSegment(sketch, "E342", {"start": v(-56.62, 10.5) * mm, "end": v(-56.7, 11.44) * mm});
            skLineSegment(sketch, "E343", {"start": v(-56.7, 11.44) * mm, "end": v(-56.85, 13.31) * mm});
            skLineSegment(sketch, "E344", {"start": v(-56.85, 13.31) * mm, "end": v(-56.98, 15.17) * mm});
            skLineSegment(sketch, "E345", {"start": v(-56.98, 15.17) * mm, "end": v(-57.1, 17.02) * mm});
            skLineSegment(sketch, "E346", {"start": v(-57.1, 17.02) * mm, "end": v(-57.24, 18.84) * mm});
            skLineSegment(sketch, "E347", {"start": v(-57.24, 18.84) * mm, "end": v(-57.32, 19.74) * mm});
            skLineSegment(sketch, "E348", {"start": v(-57.32, 19.74) * mm, "end": v(-57.4, 20.64) * mm});
            skLineSegment(sketch, "E349", {"start": v(-57.4, 20.64) * mm, "end": v(-57.5, 21.52) * mm});
            skLineSegment(sketch, "E350", {"start": v(-57.5, 21.52) * mm, "end": v(-57.6, 22.4) * mm});
            skLineSegment(sketch, "E351", {"start": v(-57.6, 22.4) * mm, "end": v(-57.73, 23.26) * mm});
            skLineSegment(sketch, "E352", {"start": v(-57.73, 23.26) * mm, "end": v(-57.86, 24.12) * mm});
            skLineSegment(sketch, "E353", {"start": v(-57.86, 24.12) * mm, "end": v(-58.02, 24.96) * mm});
            skLineSegment(sketch, "E354", {"start": v(-58.02, 24.96) * mm, "end": v(-58.18, 25.78) * mm});
            skLineSegment(sketch, "E355", {"start": v(-58.18, 25.78) * mm, "end": v(-58.37, 26.6) * mm});
            skLineSegment(sketch, "E356", {"start": v(-58.37, 26.6) * mm, "end": v(-58.58, 27.4) * mm});
            skLineSegment(sketch, "E357", {"start": v(-58.58, 27.4) * mm, "end": v(-58.82, 28.18) * mm});
            skLineSegment(sketch, "E358", {"start": v(-58.82, 28.18) * mm, "end": v(-58.94, 28.56) * mm});
            skLineSegment(sketch, "E359", {"start": v(-58.94, 28.56) * mm, "end": v(-59.08, 28.94) * mm});
            skLineSegment(sketch, "E360", {"start": v(-59.08, 28.94) * mm, "end": v(-59.22, 29.32) * mm});
            skLineSegment(sketch, "E361", {"start": v(-59.22, 29.32) * mm, "end": v(-59.36, 29.7) * mm});
            skLineSegment(sketch, "E362", {"start": v(-59.36, 29.7) * mm, "end": v(-59.52, 30.06) * mm});
            skLineSegment(sketch, "E363", {"start": v(-59.52, 30.06) * mm, "end": v(-59.68, 30.42) * mm});
            skLineSegment(sketch, "E364", {"start": v(-59.68, 30.42) * mm, "end": v(-59.84, 30.78) * mm});
            skLineSegment(sketch, "E365", {"start": v(-59.84, 30.78) * mm, "end": v(-60.02, 31.13) * mm});
            skLineSegment(sketch, "E366", {"start": v(-60.02, 31.13) * mm, "end": v(-60.2, 31.48) * mm});
            skLineSegment(sketch, "E367", {"start": v(-60.2, 31.48) * mm, "end": v(-60.4, 31.82) * mm});
            skLineSegment(sketch, "E368", {"start": v(-60.4, 31.82) * mm, "end": v(-60.56, 32.26) * mm});
            skLineSegment(sketch, "E369", {"start": v(-60.56, 32.26) * mm, "end": v(-60.71, 32.71) * mm});
            skLineSegment(sketch, "E370", {"start": v(-60.71, 32.71) * mm, "end": v(-60.84, 33.17) * mm});
            skLineSegment(sketch, "E371", {"start": v(-60.84, 33.17) * mm, "end": v(-60.95, 33.65) * mm});
            skLineSegment(sketch, "E372", {"start": v(-60.95, 33.65) * mm, "end": v(-61.03, 34.13) * mm});
            skLineSegment(sketch, "E373", {"start": v(-61.03, 34.13) * mm, "end": v(-61.09, 34.61) * mm});
            skLineSegment(sketch, "E374", {"start": v(-61.09, 34.61) * mm, "end": v(-61.13, 35.1) * mm});
            skLineSegment(sketch, "E375", {"start": v(-61.13, 35.1) * mm, "end": v(-61.14, 35.61) * mm});
            skArc(sketch, "E376", {"start": v(-61.14, 35.61) * mm, "mid": v(-58.2, 42.68) * mm, "end": v(-51.14, 45.61) * mm});
            skLineSegment(sketch, "E377", {"start": v(-51.14, 45.61) * mm, "end": v(-51.08, 45.61) * mm});
            skSolve(sketch);
        }
        {
            var Q0;
            Q0=makeQuery(id+"F0.imprint","IMPRINT",FACE,{"disambiguationData":[TD([[makeQuery(id+"F0.imprint","IMPRINT",EDGE,{"derivedFrom":sQuery(id+"F0.wireOp",EDGE,"E0")}),-1.0]])]});
            extrude(context, id + "F1", {"entities" : qUnion([Q0]), "depth" : 30 * mm, "offsetDistance" : 25 * mm});
        }
        {
            var Q0;
            Q0=makeQuery(id+"F0.imprint","IMPRINT",FACE,{"disambiguationData":[TD([[makeQuery(id+"F0.imprint","IMPRINT",EDGE,{"derivedFrom":sQuery(id+"F0.wireOp",EDGE,"E0")}),1.0]])]});
            var sketch = newSketch(context, id + "F2", { "sketchPlane" : qUnion([Q0])});
            skLineSegment(sketch, "E378.bottom", {"start": v(-42.09, 10.46) * mm, "end": v(30.77, 10.46) * mm});
            skLineSegment(sketch, "E378.top", {"start": v(-42.09, 12.54) * mm, "end": v(30.77, 12.54) * mm});
            skLineSegment(sketch, "E378.left", {"start": v(-42.09, 10.46) * mm, "end": v(-42.09, 12.54) * mm});
            skLineSegment(sketch, "E378.right", {"start": v(30.77, 10.46) * mm, "end": v(30.77, 12.54) * mm});
            skSolve(sketch);
        }
        {
            var Q0;
            {var subQ0=sQuery(id+"F2.wireOp",EDGE,"E378.bottom");var subQ1=makeQuery(id+"F0.imprint","IMPRINT",EDGE,{"derivedFrom":sQuery(id+"F0.wireOp",EDGE,"E0")});var subQ2=makeQuery(id+"F2.imprint","INTERSECT",VERTEX,{"derivedFrom":[subQ1,subQ0]});Q0=makeQuery(id+"F2.imprint","IMPRINT",FACE,{"disambiguationData":[TD([[makeQuery(id+"F2.imprint","IMPRINT",EDGE,{"disambiguationData":[TD([[subQ2,-1.0]])],"derivedFrom":subQ0}),1.0]])]});}
            extrude(context, id + "F3", {"entities" : qUnion([Q0]), "operationType" : NewBodyOperationType.ADD, "depth" : 30 * mm, "offsetDistance" : 25 * mm});
        }
        {
            var Q0;
            {var subQ0=sQuery(id+"F0.wireOp",EDGE,"E3");var subQ1=sQuery(id+"F0.wireOp",EDGE,"E0");Q0=makeQuery(id+"F3.boolean.opBoolean","MERGE",FACE,{"derivedFrom":[makeQuery(id+"F1.opExtrude","CAP_FACE",FACE,{"disambiguationData":[OSD([subQ1,sQuery(id+"F0.wireOp",EDGE,"E1"),sQuery(id+"F0.wireOp",EDGE,"E2"),subQ0,sQuery(id+"F0.wireOp",EDGE,"E4"),sQuery(id+"F0.wireOp",EDGE,"E5"),sQuery(id+"F0.wireOp",EDGE,"E6"),sQuery(id+"F0.wireOp",EDGE,"E7"),sQuery(id+"F0.wireOp",EDGE,"E8"),sQuery(id+"F0.wireOp",EDGE,"E9"),sQuery(id+"F0.wireOp",EDGE,"E10"),sQuery(id+"F0.wireOp",EDGE,"E11"),sQuery(id+"F0.wireOp",EDGE,"E12"),sQuery(id+"F0.wireOp",EDGE,"E13"),sQuery(id+"F0.wireOp",EDGE,"E14"),sQuery(id+"F0.wireOp",EDGE,"E15"),sQuery(id+"F0.wireOp",EDGE,"E16"),sQuery(id+"F0.wireOp",EDGE,"E17"),sQuery(id+"F0.wireOp",EDGE,"E18"),sQuery(id+"F0.wireOp",EDGE,"E19"),sQuery(id+"F0.wireOp",EDGE,"E20"),sQuery(id+"F0.wireOp",EDGE,"E21"),sQuery(id+"F0.wireOp",EDGE,"E22"),sQuery(id+"F0.wireOp",EDGE,"E23"),sQuery(id+"F0.wireOp",EDGE,"E24"),sQuery(id+"F0.wireOp",EDGE,"E25"),sQuery(id+"F0.wireOp",EDGE,"E26"),sQuery(id+"F0.wireOp",EDGE,"E27"),sQuery(id+"F0.wireOp",EDGE,"E28"),sQuery(id+"F0.wireOp",EDGE,"E29"),sQuery(id+"F0.wireOp",EDGE,"E30"),sQuery(id+"F0.wireOp",EDGE,"E31"),sQuery(id+"F0.wireOp",EDGE,"E32"),sQuery(id+"F0.wireOp",EDGE,"E33"),sQuery(id+"F0.wireOp",EDGE,"E34"),sQuery(id+"F0.wireOp",EDGE,"E35"),sQuery(id+"F0.wireOp",EDGE,"E36"),sQuery(id+"F0.wireOp",EDGE,"E37"),sQuery(id+"F0.wireOp",EDGE,"E38"),sQuery(id+"F0.wireOp",EDGE,"E39"),sQuery(id+"F0.wireOp",EDGE,"E40"),sQuery(id+"F0.wireOp",EDGE,"E41"),sQuery(id+"F0.wireOp",EDGE,"E42"),sQuery(id+"F0.wireOp",EDGE,"E43"),sQuery(id+"F0.wireOp",EDGE,"E44"),sQuery(id+"F0.wireOp",EDGE,"E45"),sQuery(id+"F0.wireOp",EDGE,"E46"),sQuery(id+"F0.wireOp",EDGE,"E47"),sQuery(id+"F0.wireOp",EDGE,"E48"),sQuery(id+"F0.wireOp",EDGE,"E49"),sQuery(id+"F0.wireOp",EDGE,"E50"),sQuery(id+"F0.wireOp",EDGE,"E51"),sQuery(id+"F0.wireOp",EDGE,"E52"),sQuery(id+"F0.wireOp",EDGE,"E53"),sQuery(id+"F0.wireOp",EDGE,"E54"),sQuery(id+"F0.wireOp",EDGE,"E55"),sQuery(id+"F0.wireOp",EDGE,"E56"),sQuery(id+"F0.wireOp",EDGE,"E57"),sQuery(id+"F0.wireOp",EDGE,"E58"),sQuery(id+"F0.wireOp",EDGE,"E59"),sQuery(id+"F0.wireOp",EDGE,"E60"),sQuery(id+"F0.wireOp",EDGE,"E61"),sQuery(id+"F0.wireOp",EDGE,"E62"),sQuery(id+"F0.wireOp",EDGE,"E63"),sQuery(id+"F0.wireOp",EDGE,"E64"),sQuery(id+"F0.wireOp",EDGE,"E65"),sQuery(id+"F0.wireOp",EDGE,"E66"),sQuery(id+"F0.wireOp",EDGE,"E67"),sQuery(id+"F0.wireOp",EDGE,"E68"),sQuery(id+"F0.wireOp",EDGE,"E69"),sQuery(id+"F0.wireOp",EDGE,"E70"),sQuery(id+"F0.wireOp",EDGE,"E71"),sQuery(id+"F0.wireOp",EDGE,"E72"),sQuery(id+"F0.wireOp",EDGE,"E73"),sQuery(id+"F0.wireOp",EDGE,"E74"),sQuery(id+"F0.wireOp",EDGE,"E75"),sQuery(id+"F0.wireOp",EDGE,"E76"),sQuery(id+"F0.wireOp",EDGE,"E77"),sQuery(id+"F0.wireOp",EDGE,"E78"),sQuery(id+"F0.wireOp",EDGE,"E79"),sQuery(id+"F0.wireOp",EDGE,"E80"),sQuery(id+"F0.wireOp",EDGE,"E81"),sQuery(id+"F0.wireOp",EDGE,"E82"),sQuery(id+"F0.wireOp",EDGE,"E83"),sQuery(id+"F0.wireOp",EDGE,"E84"),sQuery(id+"F0.wireOp",EDGE,"E85"),sQuery(id+"F0.wireOp",EDGE,"E86"),sQuery(id+"F0.wireOp",EDGE,"E87"),sQuery(id+"F0.wireOp",EDGE,"E88"),sQuery(id+"F0.wireOp",EDGE,"E89"),sQuery(id+"F0.wireOp",EDGE,"E90"),sQuery(id+"F0.wireOp",EDGE,"E91"),sQuery(id+"F0.wireOp",EDGE,"E92"),sQuery(id+"F0.wireOp",EDGE,"E93"),sQuery(id+"F0.wireOp",EDGE,"E94"),sQuery(id+"F0.wireOp",EDGE,"E95"),sQuery(id+"F0.wireOp",EDGE,"E96"),sQuery(id+"F0.wireOp",EDGE,"E97"),sQuery(id+"F0.wireOp",EDGE,"E98"),sQuery(id+"F0.wireOp",EDGE,"E99"),sQuery(id+"F0.wireOp",EDGE,"E100"),sQuery(id+"F0.wireOp",EDGE,"E101"),sQuery(id+"F0.wireOp",EDGE,"E102"),sQuery(id+"F0.wireOp",EDGE,"E103"),sQuery(id+"F0.wireOp",EDGE,"E104"),sQuery(id+"F0.wireOp",EDGE,"E105"),sQuery(id+"F0.wireOp",EDGE,"E106"),sQuery(id+"F0.wireOp",EDGE,"E107"),sQuery(id+"F0.wireOp",EDGE,"E108"),sQuery(id+"F0.wireOp",EDGE,"E109"),sQuery(id+"F0.wireOp",EDGE,"E110"),sQuery(id+"F0.wireOp",EDGE,"E111"),sQuery(id+"F0.wireOp",EDGE,"E112"),sQuery(id+"F0.wireOp",EDGE,"E113"),sQuery(id+"F0.wireOp",EDGE,"E114"),sQuery(id+"F0.wireOp",EDGE,"E115"),sQuery(id+"F0.wireOp",EDGE,"E116"),sQuery(id+"F0.wireOp",EDGE,"E117"),sQuery(id+"F0.wireOp",EDGE,"E118"),sQuery(id+"F0.wireOp",EDGE,"E119"),sQuery(id+"F0.wireOp",EDGE,"E120"),sQuery(id+"F0.wireOp",EDGE,"E121"),sQuery(id+"F0.wireOp",EDGE,"E122"),sQuery(id+"F0.wireOp",EDGE,"E123"),sQuery(id+"F0.wireOp",EDGE,"E124"),sQuery(id+"F0.wireOp",EDGE,"E125"),sQuery(id+"F0.wireOp",EDGE,"E126"),sQuery(id+"F0.wireOp",EDGE,"E127"),sQuery(id+"F0.wireOp",EDGE,"E128"),sQuery(id+"F0.wireOp",EDGE,"E129"),sQuery(id+"F0.wireOp",EDGE,"E130"),sQuery(id+"F0.wireOp",EDGE,"E131"),sQuery(id+"F0.wireOp",EDGE,"E132"),sQuery(id+"F0.wireOp",EDGE,"E133"),sQuery(id+"F0.wireOp",EDGE,"E134"),sQuery(id+"F0.wireOp",EDGE,"E135"),sQuery(id+"F0.wireOp",EDGE,"E136"),sQuery(id+"F0.wireOp",EDGE,"E137"),sQuery(id+"F0.wireOp",EDGE,"E138"),sQuery(id+"F0.wireOp",EDGE,"E139"),sQuery(id+"F0.wireOp",EDGE,"E140"),sQuery(id+"F0.wireOp",EDGE,"E141"),sQuery(id+"F0.wireOp",EDGE,"E142"),sQuery(id+"F0.wireOp",EDGE,"E143"),sQuery(id+"F0.wireOp",EDGE,"E144"),sQuery(id+"F0.wireOp",EDGE,"E145"),sQuery(id+"F0.wireOp",EDGE,"E146"),sQuery(id+"F0.wireOp",EDGE,"E147"),sQuery(id+"F0.wireOp",EDGE,"E148"),sQuery(id+"F0.wireOp",EDGE,"E149"),sQuery(id+"F0.wireOp",EDGE,"E150"),sQuery(id+"F0.wireOp",EDGE,"E151"),sQuery(id+"F0.wireOp",EDGE,"E152"),sQuery(id+"F0.wireOp",EDGE,"E153"),sQuery(id+"F0.wireOp",EDGE,"E154"),sQuery(id+"F0.wireOp",EDGE,"E155"),sQuery(id+"F0.wireOp",EDGE,"E156"),sQuery(id+"F0.wireOp",EDGE,"E157"),sQuery(id+"F0.wireOp",EDGE,"E158"),sQuery(id+"F0.wireOp",EDGE,"E159"),sQuery(id+"F0.wireOp",EDGE,"E160"),sQuery(id+"F0.wireOp",EDGE,"E161"),sQuery(id+"F0.wireOp",EDGE,"E162"),sQuery(id+"F0.wireOp",EDGE,"E163"),sQuery(id+"F0.wireOp",EDGE,"E164"),sQuery(id+"F0.wireOp",EDGE,"E165"),sQuery(id+"F0.wireOp",EDGE,"E166"),sQuery(id+"F0.wireOp",EDGE,"E167"),sQuery(id+"F0.wireOp",EDGE,"E168"),sQuery(id+"F0.wireOp",EDGE,"E169"),sQuery(id+"F0.wireOp",EDGE,"E170"),sQuery(id+"F0.wireOp",EDGE,"E171"),sQuery(id+"F0.wireOp",EDGE,"E172"),sQuery(id+"F0.wireOp",EDGE,"E173"),sQuery(id+"F0.wireOp",EDGE,"E174"),sQuery(id+"F0.wireOp",EDGE,"E175"),sQuery(id+"F0.wireOp",EDGE,"E176"),sQuery(id+"F0.wireOp",EDGE,"E177"),sQuery(id+"F0.wireOp",EDGE,"E178"),sQuery(id+"F0.wireOp",EDGE,"E179"),sQuery(id+"F0.wireOp",EDGE,"E180"),sQuery(id+"F0.wireOp",EDGE,"E181"),sQuery(id+"F0.wireOp",EDGE,"E182"),sQuery(id+"F0.wireOp",EDGE,"E183"),sQuery(id+"F0.wireOp",EDGE,"E184"),sQuery(id+"F0.wireOp",EDGE,"E185"),sQuery(id+"F0.wireOp",EDGE,"E186"),sQuery(id+"F0.wireOp",EDGE,"E187"),sQuery(id+"F0.wireOp",EDGE,"E188"),sQuery(id+"F0.wireOp",EDGE,"E189"),sQuery(id+"F0.wireOp",EDGE,"E190"),sQuery(id+"F0.wireOp",EDGE,"E191"),sQuery(id+"F0.wireOp",EDGE,"E192"),sQuery(id+"F0.wireOp",EDGE,"E193"),sQuery(id+"F0.wireOp",EDGE,"E194"),sQuery(id+"F0.wireOp",EDGE,"E195"),sQuery(id+"F0.wireOp",EDGE,"E196"),sQuery(id+"F0.wireOp",EDGE,"E197"),sQuery(id+"F0.wireOp",EDGE,"E198"),sQuery(id+"F0.wireOp",EDGE,"E199"),sQuery(id+"F0.wireOp",EDGE,"E200"),sQuery(id+"F0.wireOp",EDGE,"E201"),sQuery(id+"F0.wireOp",EDGE,"E202"),sQuery(id+"F0.wireOp",EDGE,"E203"),sQuery(id+"F0.wireOp",EDGE,"E204"),sQuery(id+"F0.wireOp",EDGE,"E205"),sQuery(id+"F0.wireOp",EDGE,"E206"),sQuery(id+"F0.wireOp",EDGE,"E207"),sQuery(id+"F0.wireOp",EDGE,"E208"),sQuery(id+"F0.wireOp",EDGE,"E209"),sQuery(id+"F0.wireOp",EDGE,"E210"),sQuery(id+"F0.wireOp",EDGE,"E211"),sQuery(id+"F0.wireOp",EDGE,"E212"),sQuery(id+"F0.wireOp",EDGE,"E213"),sQuery(id+"F0.wireOp",EDGE,"E214"),sQuery(id+"F0.wireOp",EDGE,"E215"),sQuery(id+"F0.wireOp",EDGE,"E216"),sQuery(id+"F0.wireOp",EDGE,"E217"),sQuery(id+"F0.wireOp",EDGE,"E218"),sQuery(id+"F0.wireOp",EDGE,"E219"),sQuery(id+"F0.wireOp",EDGE,"E220"),sQuery(id+"F0.wireOp",EDGE,"E221"),sQuery(id+"F0.wireOp",EDGE,"E222"),sQuery(id+"F0.wireOp",EDGE,"E223"),sQuery(id+"F0.wireOp",EDGE,"E224"),sQuery(id+"F0.wireOp",EDGE,"E225"),sQuery(id+"F0.wireOp",EDGE,"E226"),sQuery(id+"F0.wireOp",EDGE,"E227"),sQuery(id+"F0.wireOp",EDGE,"E228"),sQuery(id+"F0.wireOp",EDGE,"E229"),sQuery(id+"F0.wireOp",EDGE,"E230"),sQuery(id+"F0.wireOp",EDGE,"E231"),sQuery(id+"F0.wireOp",EDGE,"E232"),sQuery(id+"F0.wireOp",EDGE,"E233"),sQuery(id+"F0.wireOp",EDGE,"E234"),sQuery(id+"F0.wireOp",EDGE,"E235"),sQuery(id+"F0.wireOp",EDGE,"E236"),sQuery(id+"F0.wireOp",EDGE,"E237"),sQuery(id+"F0.wireOp",EDGE,"E238"),sQuery(id+"F0.wireOp",EDGE,"E239"),sQuery(id+"F0.wireOp",EDGE,"E240"),sQuery(id+"F0.wireOp",EDGE,"E241"),sQuery(id+"F0.wireOp",EDGE,"E242"),sQuery(id+"F0.wireOp",EDGE,"E243"),sQuery(id+"F0.wireOp",EDGE,"E244"),sQuery(id+"F0.wireOp",EDGE,"E245"),sQuery(id+"F0.wireOp",EDGE,"E246"),sQuery(id+"F0.wireOp",EDGE,"E247"),sQuery(id+"F0.wireOp",EDGE,"E248"),sQuery(id+"F0.wireOp",EDGE,"E249"),sQuery(id+"F0.wireOp",EDGE,"E250"),sQuery(id+"F0.wireOp",EDGE,"E251"),sQuery(id+"F0.wireOp",EDGE,"E252"),sQuery(id+"F0.wireOp",EDGE,"E253"),sQuery(id+"F0.wireOp",EDGE,"E254"),sQuery(id+"F0.wireOp",EDGE,"E255"),sQuery(id+"F0.wireOp",EDGE,"E256"),sQuery(id+"F0.wireOp",EDGE,"E257"),sQuery(id+"F0.wireOp",EDGE,"E258"),sQuery(id+"F0.wireOp",EDGE,"E259"),sQuery(id+"F0.wireOp",EDGE,"E260"),sQuery(id+"F0.wireOp",EDGE,"E261"),sQuery(id+"F0.wireOp",EDGE,"E262"),sQuery(id+"F0.wireOp",EDGE,"E263"),sQuery(id+"F0.wireOp",EDGE,"E264"),sQuery(id+"F0.wireOp",EDGE,"E265"),sQuery(id+"F0.wireOp",EDGE,"E266"),sQuery(id+"F0.wireOp",EDGE,"E267"),sQuery(id+"F0.wireOp",EDGE,"E268"),sQuery(id+"F0.wireOp",EDGE,"E269"),sQuery(id+"F0.wireOp",EDGE,"E270"),sQuery(id+"F0.wireOp",EDGE,"E271"),sQuery(id+"F0.wireOp",EDGE,"E272"),sQuery(id+"F0.wireOp",EDGE,"E273"),sQuery(id+"F0.wireOp",EDGE,"E274"),sQuery(id+"F0.wireOp",EDGE,"E275"),sQuery(id+"F0.wireOp",EDGE,"E276"),sQuery(id+"F0.wireOp",EDGE,"E277"),sQuery(id+"F0.wireOp",EDGE,"E278"),sQuery(id+"F0.wireOp",EDGE,"E279"),sQuery(id+"F0.wireOp",EDGE,"E280"),sQuery(id+"F0.wireOp",EDGE,"E281"),sQuery(id+"F0.wireOp",EDGE,"E282"),sQuery(id+"F0.wireOp",EDGE,"E283"),sQuery(id+"F0.wireOp",EDGE,"E284"),sQuery(id+"F0.wireOp",EDGE,"E285"),sQuery(id+"F0.wireOp",EDGE,"E286"),sQuery(id+"F0.wireOp",EDGE,"E287"),sQuery(id+"F0.wireOp",EDGE,"E288"),sQuery(id+"F0.wireOp",EDGE,"E289"),sQuery(id+"F0.wireOp",EDGE,"E290"),sQuery(id+"F0.wireOp",EDGE,"E291"),sQuery(id+"F0.wireOp",EDGE,"E292"),sQuery(id+"F0.wireOp",EDGE,"E293"),sQuery(id+"F0.wireOp",EDGE,"E294"),sQuery(id+"F0.wireOp",EDGE,"E295"),sQuery(id+"F0.wireOp",EDGE,"E296"),sQuery(id+"F0.wireOp",EDGE,"E297"),sQuery(id+"F0.wireOp",EDGE,"E298"),sQuery(id+"F0.wireOp",EDGE,"E299"),sQuery(id+"F0.wireOp",EDGE,"E300"),sQuery(id+"F0.wireOp",EDGE,"E301"),sQuery(id+"F0.wireOp",EDGE,"E302"),sQuery(id+"F0.wireOp",EDGE,"E303"),sQuery(id+"F0.wireOp",EDGE,"E304"),sQuery(id+"F0.wireOp",EDGE,"E305"),sQuery(id+"F0.wireOp",EDGE,"E306"),sQuery(id+"F0.wireOp",EDGE,"E307"),sQuery(id+"F0.wireOp",EDGE,"E308"),sQuery(id+"F0.wireOp",EDGE,"E309"),sQuery(id+"F0.wireOp",EDGE,"E310"),sQuery(id+"F0.wireOp",EDGE,"E311"),sQuery(id+"F0.wireOp",EDGE,"E312"),sQuery(id+"F0.wireOp",EDGE,"E313"),sQuery(id+"F0.wireOp",EDGE,"E314"),sQuery(id+"F0.wireOp",EDGE,"E315"),sQuery(id+"F0.wireOp",EDGE,"E316"),sQuery(id+"F0.wireOp",EDGE,"E317"),sQuery(id+"F0.wireOp",EDGE,"E318"),sQuery(id+"F0.wireOp",EDGE,"E319"),sQuery(id+"F0.wireOp",EDGE,"E320"),sQuery(id+"F0.wireOp",EDGE,"E321"),sQuery(id+"F0.wireOp",EDGE,"E322"),sQuery(id+"F0.wireOp",EDGE,"E323"),sQuery(id+"F0.wireOp",EDGE,"E324"),sQuery(id+"F0.wireOp",EDGE,"E325"),sQuery(id+"F0.wireOp",EDGE,"E326"),sQuery(id+"F0.wireOp",EDGE,"E327"),sQuery(id+"F0.wireOp",EDGE,"E328"),sQuery(id+"F0.wireOp",EDGE,"E329"),sQuery(id+"F0.wireOp",EDGE,"E330"),sQuery(id+"F0.wireOp",EDGE,"E331"),sQuery(id+"F0.wireOp",EDGE,"E332"),sQuery(id+"F0.wireOp",EDGE,"E333"),sQuery(id+"F0.wireOp",EDGE,"E334"),sQuery(id+"F0.wireOp",EDGE,"E335"),sQuery(id+"F0.wireOp",EDGE,"E336"),sQuery(id+"F0.wireOp",EDGE,"E337"),sQuery(id+"F0.wireOp",EDGE,"E338"),sQuery(id+"F0.wireOp",EDGE,"E339"),sQuery(id+"F0.wireOp",EDGE,"E340"),sQuery(id+"F0.wireOp",EDGE,"E341"),sQuery(id+"F0.wireOp",EDGE,"E342"),sQuery(id+"F0.wireOp",EDGE,"E343"),sQuery(id+"F0.wireOp",EDGE,"E344"),sQuery(id+"F0.wireOp",EDGE,"E345"),sQuery(id+"F0.wireOp",EDGE,"E346"),sQuery(id+"F0.wireOp",EDGE,"E347"),sQuery(id+"F0.wireOp",EDGE,"E348"),sQuery(id+"F0.wireOp",EDGE,"E349"),sQuery(id+"F0.wireOp",EDGE,"E350"),sQuery(id+"F0.wireOp",EDGE,"E351"),sQuery(id+"F0.wireOp",EDGE,"E352"),sQuery(id+"F0.wireOp",EDGE,"E353"),sQuery(id+"F0.wireOp",EDGE,"E354"),sQuery(id+"F0.wireOp",EDGE,"E355"),sQuery(id+"F0.wireOp",EDGE,"E356"),sQuery(id+"F0.wireOp",EDGE,"E357"),sQuery(id+"F0.wireOp",EDGE,"E358"),sQuery(id+"F0.wireOp",EDGE,"E359"),sQuery(id+"F0.wireOp",EDGE,"E360"),sQuery(id+"F0.wireOp",EDGE,"E361"),sQuery(id+"F0.wireOp",EDGE,"E362"),sQuery(id+"F0.wireOp",EDGE,"E363"),sQuery(id+"F0.wireOp",EDGE,"E364"),sQuery(id+"F0.wireOp",EDGE,"E365"),sQuery(id+"F0.wireOp",EDGE,"E366"),sQuery(id+"F0.wireOp",EDGE,"E367"),sQuery(id+"F0.wireOp",EDGE,"E368"),sQuery(id+"F0.wireOp",EDGE,"E369"),sQuery(id+"F0.wireOp",EDGE,"E370"),sQuery(id+"F0.wireOp",EDGE,"E371"),sQuery(id+"F0.wireOp",EDGE,"E372"),sQuery(id+"F0.wireOp",EDGE,"E373"),sQuery(id+"F0.wireOp",EDGE,"E374"),sQuery(id+"F0.wireOp",EDGE,"E375"),sQuery(id+"F0.wireOp",EDGE,"E376")])],"isStart":false}),makeQuery(id+"F3.opExtrude","CAP_FACE",FACE,{"disambiguationData":[OSD([subQ1,subQ0,sQuery(id+"F2.wireOp",EDGE,"E378.bottom"),sQuery(id+"F2.wireOp",EDGE,"E378.top")])],"isStart":false})]});}
            var sketch = newSketch(context, id + "F4", { "sketchPlane" : qUnion([Q0])});
            skLineSegment(sketch, "E379", {"start": v(-40.62, 11.64) * mm, "end": v(26.87, 11.64) * mm});
            skArc(sketch, "E380", {"start": v(26.87, 11.64) * mm, "mid": v(-6.88, 45.12) * mm, "end": v(-40.62, 11.64) * mm});
            skSolve(sketch);
        }
        {
            var Q0;
            Q0=makeQuery(id+"F4.imprint","IMPRINT",FACE,{"disambiguationData":[TD([[makeQuery(id+"F4.imprint","IMPRINT",EDGE,{"derivedFrom":sQuery(id+"F4.wireOp",EDGE,"E379")}),1.0]])]});
            var Q1;
            {var subQ0=sQuery(id+"F2.wireOp",EDGE,"E378.top");Q1=makeQuery(id+"F4.imprint","IMPRINT",FACE,{"disambiguationData":[TD([[makeQuery(id+"F4.imprint","IMPRINT",EDGE,{"derivedFrom":makeQuery(id+"F3.opExtrude","CAP_EDGE",EDGE,{"disambiguationData":[OSD([subQ0])],"isStart":false})}),1.0]])]});}
            extrude(context, id + "F5", {"entities" : qUnion([Q0, Q1]), "operationType" : NewBodyOperationType.ADD, "oppositeDirection" : true, "depth" : 3 * mm, "offsetDistance" : 25 * mm});
        }
    });
